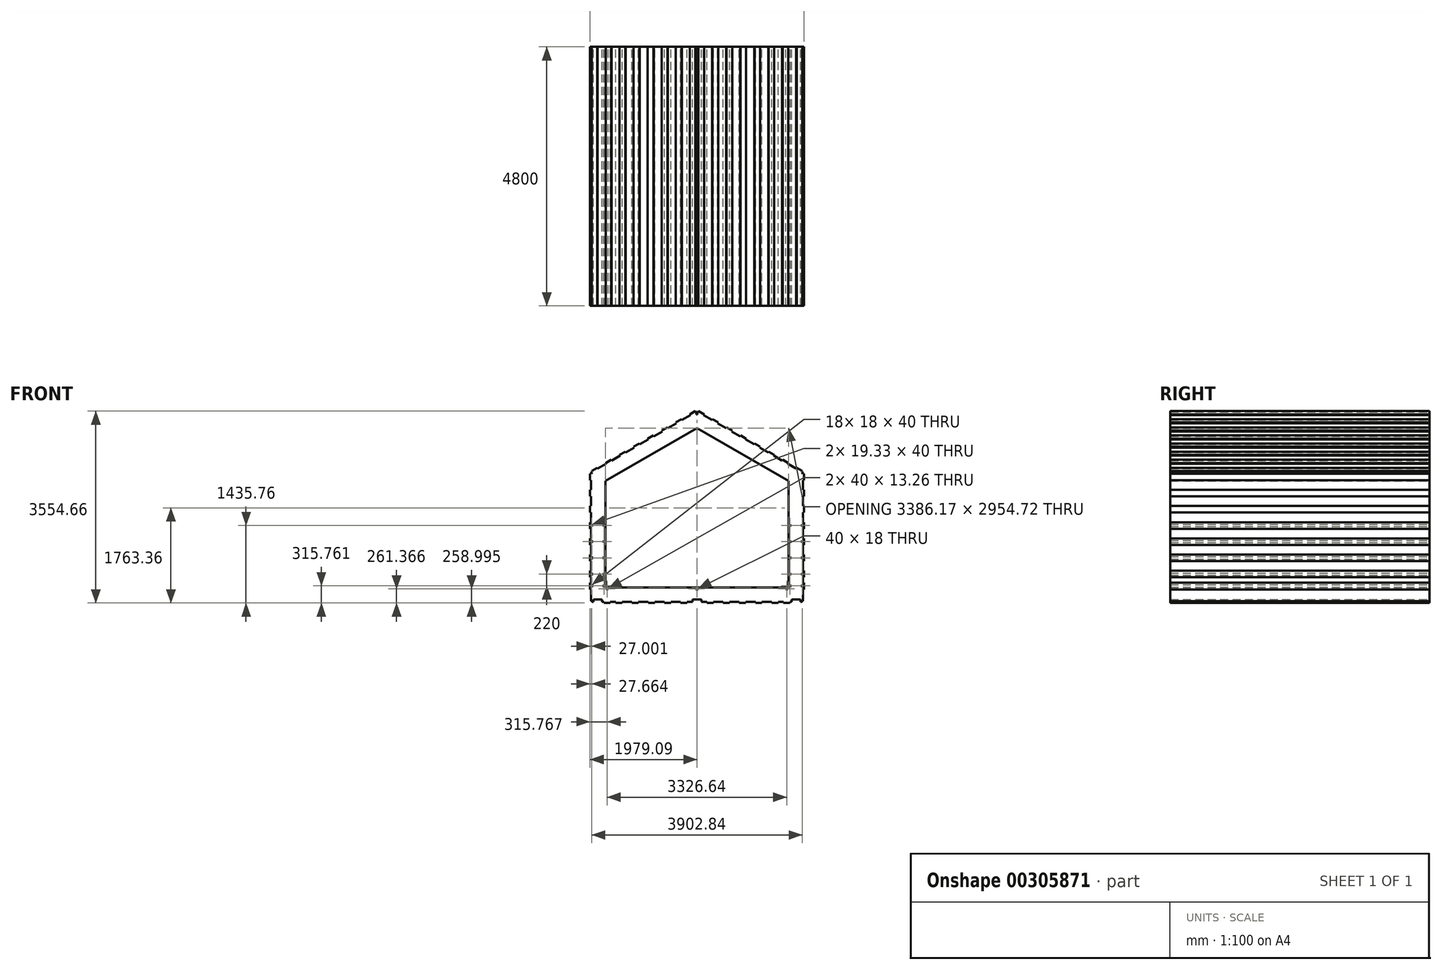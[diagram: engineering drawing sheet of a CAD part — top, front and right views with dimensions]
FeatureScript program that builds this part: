
annotation { "Feature Type Name" : "Feature", "Feature Type Description" : "" }
export const myFeature = defineFeature(function(context is Context, id is Id, definition is map)
    precondition{}
    {
        {
            var Q0;
            Q0=qCreatedBy(makeId("Front.planeOp"),FACE);
            var sketch = newSketch(context, id + "F0", { "sketchPlane" : qUnion([Q0])});
            skLineSegment(sketch, "E0", {"start": v(-1672.1, -978.06) * mm, "end": v(-1672.1, -1067.82) * mm});
            skLineSegment(sketch, "E1", {"start": v(-1672.1, -1067.82) * mm, "end": v(-1582.33, -1067.82) * mm});
            skLineSegment(sketch, "E2", {"start": v(-1582.33, -1067.82) * mm, "end": v(-1582.33, -1085.82) * mm});
            skLineSegment(sketch, "E3", {"start": v(-1582.33, -1085.82) * mm, "end": v(-1482.33, -1085.82) * mm});
            skLineSegment(sketch, "E4", {"start": v(-1482.33, -1085.82) * mm, "end": v(-1482.33, -1067.82) * mm});
            skLineSegment(sketch, "E5", {"start": v(-1482.33, -1067.82) * mm, "end": v(-1362.33, -1067.82) * mm});
            skLineSegment(sketch, "E6", {"start": v(-1362.33, -1067.82) * mm, "end": v(-1362.33, -1085.82) * mm});
            skLineSegment(sketch, "E7", {"start": v(-1362.33, -1085.82) * mm, "end": v(-1182.33, -1085.82) * mm});
            skLineSegment(sketch, "E8", {"start": v(-1182.33, -1085.82) * mm, "end": v(-1182.33, -1067.82) * mm});
            skLineSegment(sketch, "E9", {"start": v(-1182.33, -1067.82) * mm, "end": v(-1062.33, -1067.82) * mm});
            skLineSegment(sketch, "E10", {"start": v(-1062.33, -1067.82) * mm, "end": v(-1062.33, -1085.82) * mm});
            skLineSegment(sketch, "E11", {"start": v(-1062.33, -1085.82) * mm, "end": v(-882.33, -1085.82) * mm});
            skLineSegment(sketch, "E12", {"start": v(-882.33, -1085.82) * mm, "end": v(-882.33, -1067.82) * mm});
            skLineSegment(sketch, "E13", {"start": v(-882.33, -1067.82) * mm, "end": v(-762.33, -1067.82) * mm});
            skLineSegment(sketch, "E14", {"start": v(-762.33, -1067.82) * mm, "end": v(-762.33, -1085.82) * mm});
            skLineSegment(sketch, "E15", {"start": v(-762.33, -1085.82) * mm, "end": v(-582.33, -1085.82) * mm});
            skLineSegment(sketch, "E16", {"start": v(-582.33, -1085.82) * mm, "end": v(-582.33, -1067.82) * mm});
            skLineSegment(sketch, "E17", {"start": v(-582.33, -1067.82) * mm, "end": v(-462.33, -1067.82) * mm});
            skLineSegment(sketch, "E18", {"start": v(-462.33, -1067.82) * mm, "end": v(-462.33, -1085.82) * mm});
            skLineSegment(sketch, "E19", {"start": v(-462.33, -1085.82) * mm, "end": v(-282.33, -1085.82) * mm});
            skLineSegment(sketch, "E20", {"start": v(-282.33, -1085.82) * mm, "end": v(-282.33, -1067.82) * mm});
            skLineSegment(sketch, "E21", {"start": v(-282.33, -1067.82) * mm, "end": v(-162.33, -1067.82) * mm});
            skLineSegment(sketch, "E22", {"start": v(-162.33, -1067.82) * mm, "end": v(-162.33, -1085.82) * mm});
            skLineSegment(sketch, "E23", {"start": v(-162.33, -1085.82) * mm, "end": v(-39.02, -1085.82) * mm});
            skLineSegment(sketch, "E24", {"start": v(-39.02, -1085.82) * mm, "end": v(-39.02, -1067.82) * mm});
            skLineSegment(sketch, "E25", {"start": v(-39.02, -1067.82) * mm, "end": v(20.98, -1067.82) * mm});
            skLineSegment(sketch, "E26.bottom", {"start": v(0.98, -1085.82) * mm, "end": v(20.98, -1085.82) * mm});
            skLineSegment(sketch, "E26.top", {"start": v(0.98, -1103.82) * mm, "end": v(20.98, -1103.82) * mm});
            skLineSegment(sketch, "E26.left", {"start": v(0.98, -1085.82) * mm, "end": v(0.98, -1103.82) * mm});
            skLineSegment(sketch, "E26.right", {"start": v(20.98, -1085.82) * mm, "end": v(20.98, -1103.82) * mm});
            skLineSegment(sketch, "E27", {"start": v(-1672.1, -978.06) * mm, "end": v(-1690.1, -978.06) * mm});
            skLineSegment(sketch, "E28", {"start": v(-1690.1, -978.06) * mm, "end": v(-1690.1, -878.06) * mm});
            skLineSegment(sketch, "E29", {"start": v(-1690.1, -878.06) * mm, "end": v(-1672.1, -878.06) * mm});
            skLineSegment(sketch, "E30", {"start": v(-1672.1, -878.06) * mm, "end": v(-1672.1, -758.06) * mm});
            skLineSegment(sketch, "E31", {"start": v(-1672.1, -758.06) * mm, "end": v(-1690.1, -758.06) * mm});
            skLineSegment(sketch, "E32", {"start": v(-1690.1, -758.06) * mm, "end": v(-1690.1, -578.06) * mm});
            skLineSegment(sketch, "E33", {"start": v(-1690.1, -578.06) * mm, "end": v(-1672.1, -578.06) * mm});
            skLineSegment(sketch, "E34", {"start": v(-1672.1, -578.06) * mm, "end": v(-1672.1, -458.06) * mm});
            skLineSegment(sketch, "E35", {"start": v(-1672.1, -458.06) * mm, "end": v(-1690.1, -458.06) * mm});
            skLineSegment(sketch, "E36", {"start": v(-1690.1, -458.06) * mm, "end": v(-1690.1, -278.06) * mm});
            skLineSegment(sketch, "E37.bottom", {"start": v(-1690.1, -1018.06) * mm, "end": v(-1708.1, -1018.06) * mm});
            skLineSegment(sketch, "E37.top", {"start": v(-1690.1, -1058.06) * mm, "end": v(-1708.1, -1058.06) * mm});
            skLineSegment(sketch, "E37.left", {"start": v(-1690.1, -1018.06) * mm, "end": v(-1690.1, -1058.06) * mm});
            skLineSegment(sketch, "E37.right", {"start": v(-1708.1, -1018.06) * mm, "end": v(-1708.1, -1058.06) * mm});
            skLineSegment(sketch, "E38.bottom", {"start": v(-1622.33, -1085.82) * mm, "end": v(-1662.33, -1085.82) * mm});
            skLineSegment(sketch, "E38.top", {"start": v(-1622.33, -1099.08) * mm, "end": v(-1662.33, -1099.08) * mm});
            skLineSegment(sketch, "E38.left", {"start": v(-1622.33, -1085.82) * mm, "end": v(-1622.33, -1099.08) * mm});
            skLineSegment(sketch, "E38.right", {"start": v(-1662.33, -1085.82) * mm, "end": v(-1662.33, -1099.08) * mm});
            skLineSegment(sketch, "E39", {"start": v(-1690.1, -978.06) * mm, "end": v(-1940.1, -978.06) * mm, "construction": true});
            skLineSegment(sketch, "E40", {"start": v(-1940.1, -978.06) * mm, "end": v(-1958.1, -978.06) * mm});
            skLineSegment(sketch, "E41", {"start": v(-1958.1, -978.06) * mm, "end": v(-1958.1, -1103.83) * mm});
            skLineSegment(sketch, "E42", {"start": v(-1940.1, -978.06) * mm, "end": v(-1940.1, -878.06) * mm});
            skLineSegment(sketch, "E43", {"start": v(-1940.1, -878.06) * mm, "end": v(-1958.1, -878.06) * mm});
            skLineSegment(sketch, "E44.bottom", {"start": v(-1940.1, -1018.06) * mm, "end": v(-1922.1, -1018.06) * mm});
            skLineSegment(sketch, "E44.top", {"start": v(-1940.1, -1058.06) * mm, "end": v(-1922.1, -1058.06) * mm});
            skLineSegment(sketch, "E44.left", {"start": v(-1940.1, -1018.06) * mm, "end": v(-1940.1, -1058.06) * mm});
            skLineSegment(sketch, "E44.right", {"start": v(-1922.1, -1018.06) * mm, "end": v(-1922.1, -1058.06) * mm});
            skLineSegment(sketch, "E45", {"start": v(-1958.1, -878.06) * mm, "end": v(-1958.1, -758.06) * mm});
            skLineSegment(sketch, "E46", {"start": v(-1958.1, -758.06) * mm, "end": v(-1940.1, -758.06) * mm});
            skLineSegment(sketch, "E47.bottom", {"start": v(-1940.1, -838.06) * mm, "end": v(-1922.1, -838.06) * mm});
            skLineSegment(sketch, "E47.top", {"start": v(-1940.1, -798.06) * mm, "end": v(-1922.1, -798.06) * mm});
            skLineSegment(sketch, "E47.left", {"start": v(-1940.1, -838.06) * mm, "end": v(-1940.1, -798.06) * mm});
            skLineSegment(sketch, "E47.right", {"start": v(-1922.1, -838.06) * mm, "end": v(-1922.1, -798.06) * mm});
            skLineSegment(sketch, "E48", {"start": v(-1940.1, -758.06) * mm, "end": v(-1940.1, -578.06) * mm});
            skLineSegment(sketch, "E49", {"start": v(-1940.1, -578.06) * mm, "end": v(-1958.1, -578.06) * mm});
            skLineSegment(sketch, "E50.bottom", {"start": v(-1690.1, -798.06) * mm, "end": v(-1708.1, -798.06) * mm});
            skLineSegment(sketch, "E50.top", {"start": v(-1690.1, -838.06) * mm, "end": v(-1708.1, -838.06) * mm});
            skLineSegment(sketch, "E50.left", {"start": v(-1690.1, -798.06) * mm, "end": v(-1690.1, -838.06) * mm});
            skLineSegment(sketch, "E50.right", {"start": v(-1708.1, -798.06) * mm, "end": v(-1708.1, -838.06) * mm});
            skLineSegment(sketch, "E51", {"start": v(-1958.1, -578.06) * mm, "end": v(-1958.1, -458.06) * mm});
            skLineSegment(sketch, "E52", {"start": v(-1958.1, -458.06) * mm, "end": v(-1940.1, -458.06) * mm});
            skLineSegment(sketch, "E53", {"start": v(-1940.1, -458.06) * mm, "end": v(-1940.1, -278.06) * mm});
            skLineSegment(sketch, "E54.bottom", {"start": v(-1940.1, -538.06) * mm, "end": v(-1922.1, -538.06) * mm});
            skLineSegment(sketch, "E54.top", {"start": v(-1940.1, -498.06) * mm, "end": v(-1922.1, -498.06) * mm});
            skLineSegment(sketch, "E54.left", {"start": v(-1940.1, -538.06) * mm, "end": v(-1940.1, -498.06) * mm});
            skLineSegment(sketch, "E54.right", {"start": v(-1922.1, -538.06) * mm, "end": v(-1922.1, -498.06) * mm});
            skLineSegment(sketch, "E55.bottom", {"start": v(-1690.1, -538.06) * mm, "end": v(-1708.1, -538.06) * mm});
            skLineSegment(sketch, "E55.top", {"start": v(-1690.1, -498.06) * mm, "end": v(-1708.1, -498.06) * mm});
            skLineSegment(sketch, "E55.left", {"start": v(-1690.1, -538.06) * mm, "end": v(-1690.1, -498.06) * mm});
            skLineSegment(sketch, "E55.right", {"start": v(-1708.1, -538.06) * mm, "end": v(-1708.1, -498.06) * mm});
            skLineSegment(sketch, "E56", {"start": v(-1940.1, -278.06) * mm, "end": v(-1958.1, -278.06) * mm});
            skLineSegment(sketch, "E57", {"start": v(-1958.1, -278.06) * mm, "end": v(-1958.1, -158.06) * mm});
            skLineSegment(sketch, "E58", {"start": v(-1690.1, -278.06) * mm, "end": v(-1672.1, -278.06) * mm});
            skLineSegment(sketch, "E59", {"start": v(-1672.1, -278.06) * mm, "end": v(-1672.1, -158.06) * mm});
            skLineSegment(sketch, "E60.bottom", {"start": v(-1940.1, -238.06) * mm, "end": v(-1922.1, -238.06) * mm});
            skLineSegment(sketch, "E60.top", {"start": v(-1940.1, -198.06) * mm, "end": v(-1922.1, -198.06) * mm});
            skLineSegment(sketch, "E60.left", {"start": v(-1940.1, -238.06) * mm, "end": v(-1940.1, -198.06) * mm});
            skLineSegment(sketch, "E60.right", {"start": v(-1922.1, -238.06) * mm, "end": v(-1922.1, -198.06) * mm});
            skLineSegment(sketch, "E61.bottom", {"start": v(-1690.1, -238.06) * mm, "end": v(-1708.1, -238.06) * mm});
            skLineSegment(sketch, "E61.top", {"start": v(-1690.1, -198.06) * mm, "end": v(-1708.1, -198.06) * mm});
            skLineSegment(sketch, "E61.left", {"start": v(-1690.1, -238.06) * mm, "end": v(-1690.1, -198.06) * mm});
            skLineSegment(sketch, "E61.right", {"start": v(-1708.1, -238.06) * mm, "end": v(-1708.1, -198.06) * mm});
            skLineSegment(sketch, "E62", {"start": v(-1958.1, -158.06) * mm, "end": v(-1940.1, -158.06) * mm});
            skPoint(sketch, "E62.endSnap0", {"position": v(-1940.1, -218.06) * mm});
            skLineSegment(sketch, "E63", {"start": v(-1672.1, -158.06) * mm, "end": v(-1690.1, -158.06) * mm});
            skPoint(sketch, "E63.endSnap0", {"position": v(-1690.1, -218.06) * mm});
            skLineSegment(sketch, "E64", {"start": v(-1940.1, -158.06) * mm, "end": v(-1940.1, 21.94) * mm});
            skLineSegment(sketch, "E65", {"start": v(-1690.1, -158.06) * mm, "end": v(-1690.1, 21.94) * mm});
            skLineSegment(sketch, "E66", {"start": v(-1690.1, 21.94) * mm, "end": v(-1672.1, 21.94) * mm});
            skLineSegment(sketch, "E67", {"start": v(-1672.1, 21.94) * mm, "end": v(-1672.1, 141.94) * mm});
            skLineSegment(sketch, "E68", {"start": v(-1672.1, 141.94) * mm, "end": v(-1690.1, 141.94) * mm});
            skLineSegment(sketch, "E69", {"start": v(-1690.1, 141.94) * mm, "end": v(-1690.1, 321.94) * mm});
            skLineSegment(sketch, "E70", {"start": v(-1940.1, 21.94) * mm, "end": v(-1958.1, 21.94) * mm});
            skLineSegment(sketch, "E71", {"start": v(-1958.1, 21.94) * mm, "end": v(-1958.1, 141.94) * mm});
            skLineSegment(sketch, "E72", {"start": v(-1958.1, 141.94) * mm, "end": v(-1940.1, 141.94) * mm});
            skLineSegment(sketch, "E73", {"start": v(-1940.1, 141.94) * mm, "end": v(-1940.1, 321.94) * mm});
            skLineSegment(sketch, "E74.bottom", {"start": v(-1940.1, 61.94) * mm, "end": v(-1920.77, 61.94) * mm});
            skLineSegment(sketch, "E74.top", {"start": v(-1940.1, 101.94) * mm, "end": v(-1920.77, 101.94) * mm});
            skLineSegment(sketch, "E74.left", {"start": v(-1940.1, 61.94) * mm, "end": v(-1940.1, 101.94) * mm});
            skLineSegment(sketch, "E74.right", {"start": v(-1920.77, 61.94) * mm, "end": v(-1920.77, 101.94) * mm});
            skLineSegment(sketch, "E75.bottom", {"start": v(-1690.1, 61.94) * mm, "end": v(-1708.1, 61.94) * mm});
            skLineSegment(sketch, "E75.top", {"start": v(-1690.1, 101.94) * mm, "end": v(-1708.1, 101.94) * mm});
            skLineSegment(sketch, "E75.left", {"start": v(-1690.1, 61.94) * mm, "end": v(-1690.1, 101.94) * mm});
            skLineSegment(sketch, "E75.right", {"start": v(-1708.1, 61.94) * mm, "end": v(-1708.1, 101.94) * mm});
            skLineSegment(sketch, "E76", {"start": v(-1940.1, 321.94) * mm, "end": v(-1958.1, 321.94) * mm});
            skLineSegment(sketch, "E77", {"start": v(-1958.1, 321.94) * mm, "end": v(-1958.1, 441.94) * mm});
            skLineSegment(sketch, "E78", {"start": v(-1690.1, 321.94) * mm, "end": v(-1672.1, 321.94) * mm});
            skLineSegment(sketch, "E79", {"start": v(-1672.1, 321.94) * mm, "end": v(-1672.1, 441.94) * mm});
            skLineSegment(sketch, "E80", {"start": v(-1958.1, 441.94) * mm, "end": v(-1940.1, 441.94) * mm});
            skLineSegment(sketch, "E81", {"start": v(-1940.1, 441.94) * mm, "end": v(-1940.1, 621.94) * mm});
            skLineSegment(sketch, "E82", {"start": v(-1672.1, 441.94) * mm, "end": v(-1690.1, 441.94) * mm});
            skLineSegment(sketch, "E83", {"start": v(-1690.1, 441.94) * mm, "end": v(-1690.1, 621.94) * mm});
            skLineSegment(sketch, "E84", {"start": v(-1940.1, 621.94) * mm, "end": v(-1958.1, 621.94) * mm});
            skLineSegment(sketch, "E85", {"start": v(-1958.1, 621.94) * mm, "end": v(-1958.1, 741.94) * mm});
            skLineSegment(sketch, "E86", {"start": v(-1958.1, 741.94) * mm, "end": v(-1940.1, 741.94) * mm});
            skLineSegment(sketch, "E87", {"start": v(-1690.1, 621.94) * mm, "end": v(-1672.1, 621.94) * mm});
            skLineSegment(sketch, "E88", {"start": v(-1672.1, 621.94) * mm, "end": v(-1672.1, 741.94) * mm});
            skLineSegment(sketch, "E89", {"start": v(-1672.1, 741.94) * mm, "end": v(-1690.1, 741.94) * mm});
            skLineSegment(sketch, "E90", {"start": v(-1940.1, 741.94) * mm, "end": v(-1940.1, 921.94) * mm});
            skLineSegment(sketch, "E91", {"start": v(-1940.1, 921.94) * mm, "end": v(-1958.1, 921.94) * mm});
            skLineSegment(sketch, "E92", {"start": v(-1958.1, 921.94) * mm, "end": v(-1958.1, 1041.94) * mm});
            skLineSegment(sketch, "E93", {"start": v(-1958.1, 1041.94) * mm, "end": v(-1940.1, 1041.94) * mm});
            skLineSegment(sketch, "E94", {"start": v(-1940.1, 1041.94) * mm, "end": v(-1940.1, 1064.17) * mm});
            skLineSegment(sketch, "E95", {"start": v(-1940.1, 1041.94) * mm, "end": v(-1920.84, 1075.29) * mm});
            skLineSegment(sketch, "E96", {"start": v(-1940.1, 1064.17) * mm, "end": v(-1920.84, 1075.29) * mm});
            skLineSegment(sketch, "E97", {"start": v(-1920.84, 1075.29) * mm, "end": v(-1929.84, 1090.88) * mm});
            skLineSegment(sketch, "E98", {"start": v(-1929.84, 1090.88) * mm, "end": v(-1825.92, 1150.87) * mm});
            skLineSegment(sketch, "E99", {"start": v(-1825.92, 1150.87) * mm, "end": v(-1816.92, 1135.28) * mm});
            skLineSegment(sketch, "E100", {"start": v(-1816.92, 1135.28) * mm, "end": v(-1661.03, 1225.28) * mm});
            skLineSegment(sketch, "E101", {"start": v(-1661.03, 1225.28) * mm, "end": v(-1670.03, 1240.87) * mm});
            skLineSegment(sketch, "E102", {"start": v(-1670.03, 1240.87) * mm, "end": v(-1566.1, 1300.87) * mm});
            skLineSegment(sketch, "E103", {"start": v(-1566.1, 1300.87) * mm, "end": v(-1557.1, 1285.28) * mm});
            skLineSegment(sketch, "E104", {"start": v(-1661.03, 1225.28) * mm, "end": v(-1536.04, 1008.77) * mm, "construction": true});
            skLineSegment(sketch, "E105", {"start": v(-1536.04, 1008.77) * mm, "end": v(-1527.04, 993.18) * mm});
            skLineSegment(sketch, "E106", {"start": v(-1527.04, 993.18) * mm, "end": v(-1423.11, 1053.18) * mm});
            skLineSegment(sketch, "E107", {"start": v(-1423.11, 1053.18) * mm, "end": v(-1432.11, 1068.77) * mm});
            skLineSegment(sketch, "E108", {"start": v(-1690.1, 741.94) * mm, "end": v(-1690.1, 919.83) * mm});
            skLineSegment(sketch, "E109", {"start": v(-1536.04, 1008.77) * mm, "end": v(-1690.1, 919.83) * mm});
            skLineSegment(sketch, "E110", {"start": v(-1557.1, 1285.28) * mm, "end": v(-1401.22, 1375.28) * mm});
            skLineSegment(sketch, "E111", {"start": v(-1432.11, 1068.77) * mm, "end": v(-1276.23, 1158.77) * mm});
            skLineSegment(sketch, "E112", {"start": v(-1401.22, 1375.28) * mm, "end": v(-1410.22, 1390.86) * mm});
            skLineSegment(sketch, "E113", {"start": v(-1410.22, 1390.86) * mm, "end": v(-1306.3, 1450.86) * mm});
            skLineSegment(sketch, "E114", {"start": v(-1276.23, 1158.77) * mm, "end": v(-1267.23, 1143.18) * mm});
            skLineSegment(sketch, "E115", {"start": v(-1267.23, 1143.18) * mm, "end": v(-1163.3, 1203.18) * mm});
            skLineSegment(sketch, "E116", {"start": v(-1163.3, 1203.18) * mm, "end": v(-1172.3, 1218.77) * mm});
            skLineSegment(sketch, "E117", {"start": v(-1172.3, 1218.77) * mm, "end": v(-1016.42, 1308.76) * mm});
            skLineSegment(sketch, "E118", {"start": v(-1306.3, 1450.86) * mm, "end": v(-1297.3, 1435.27) * mm});
            skLineSegment(sketch, "E119", {"start": v(-1297.3, 1435.27) * mm, "end": v(-1141.41, 1525.27) * mm});
            skLineSegment(sketch, "E120", {"start": v(-1141.41, 1525.27) * mm, "end": v(-1150.41, 1540.86) * mm});
            skLineSegment(sketch, "E121", {"start": v(-1150.41, 1540.86) * mm, "end": v(-1046.49, 1600.86) * mm});
            skLineSegment(sketch, "E122", {"start": v(-1016.42, 1308.76) * mm, "end": v(-1007.42, 1293.17) * mm});
            skLineSegment(sketch, "E123", {"start": v(-1007.42, 1293.17) * mm, "end": v(-903.5, 1353.17) * mm});
            skLineSegment(sketch, "E124", {"start": v(-1046.49, 1600.86) * mm, "end": v(-1037.49, 1585.27) * mm});
            skLineSegment(sketch, "E125", {"start": v(-1037.49, 1585.27) * mm, "end": v(-881.6, 1675.27) * mm});
            skLineSegment(sketch, "E126", {"start": v(-903.5, 1353.17) * mm, "end": v(-912.5, 1368.76) * mm});
            skLineSegment(sketch, "E127", {"start": v(-912.5, 1368.76) * mm, "end": v(-756.6, 1458.76) * mm});
            skLineSegment(sketch, "E128", {"start": v(-881.6, 1675.27) * mm, "end": v(-890.6, 1690.85) * mm});
            skLineSegment(sketch, "E129", {"start": v(-890.6, 1690.85) * mm, "end": v(-786.68, 1750.85) * mm});
            skLineSegment(sketch, "E130", {"start": v(-756.6, 1458.76) * mm, "end": v(-747.6, 1443.17) * mm});
            skLineSegment(sketch, "E131", {"start": v(-747.6, 1443.17) * mm, "end": v(-643.68, 1503.17) * mm});
            skLineSegment(sketch, "E132", {"start": v(-786.68, 1750.85) * mm, "end": v(-777.68, 1735.26) * mm});
            skLineSegment(sketch, "E133", {"start": v(-777.68, 1735.26) * mm, "end": v(-621.8, 1825.26) * mm});
            skLineSegment(sketch, "E134", {"start": v(-621.8, 1825.26) * mm, "end": v(-630.8, 1840.85) * mm});
            skLineSegment(sketch, "E135", {"start": v(-630.8, 1840.85) * mm, "end": v(-526.87, 1900.85) * mm});
            skLineSegment(sketch, "E136", {"start": v(-526.87, 1900.85) * mm, "end": v(-517.87, 1885.26) * mm});
            skLineSegment(sketch, "E137", {"start": v(-517.87, 1885.26) * mm, "end": v(-361.98, 1975.26) * mm});
            skLineSegment(sketch, "E138", {"start": v(-361.98, 1975.26) * mm, "end": v(-370.98, 1990.84) * mm});
            skLineSegment(sketch, "E139", {"start": v(-370.98, 1990.84) * mm, "end": v(-267.06, 2050.84) * mm});
            skLineSegment(sketch, "E140", {"start": v(-267.06, 2050.84) * mm, "end": v(-258.06, 2035.25) * mm});
            skLineSegment(sketch, "E141", {"start": v(-258.06, 2035.25) * mm, "end": v(-102.17, 2125.25) * mm});
            skLineSegment(sketch, "E142", {"start": v(-102.17, 2125.25) * mm, "end": v(-111.17, 2140.84) * mm});
            skLineSegment(sketch, "E143", {"start": v(-111.17, 2140.84) * mm, "end": v(-7.25, 2200.84) * mm});
            skLineSegment(sketch, "E144", {"start": v(-643.68, 1503.17) * mm, "end": v(-652.68, 1518.75) * mm});
            skLineSegment(sketch, "E145", {"start": v(-652.68, 1518.75) * mm, "end": v(-496.8, 1608.75) * mm});
            skLineSegment(sketch, "E146", {"start": v(-496.8, 1608.75) * mm, "end": v(-487.8, 1593.16) * mm});
            skLineSegment(sketch, "E147", {"start": v(-487.8, 1593.16) * mm, "end": v(-383.87, 1653.16) * mm});
            skLineSegment(sketch, "E148", {"start": v(-383.87, 1653.16) * mm, "end": v(-392.87, 1668.75) * mm});
            skLineSegment(sketch, "E149", {"start": v(-392.87, 1668.75) * mm, "end": v(-236.99, 1758.75) * mm});
            skLineSegment(sketch, "E150", {"start": v(-236.99, 1758.75) * mm, "end": v(-227.99, 1743.16) * mm});
            skLineSegment(sketch, "E151", {"start": v(-227.99, 1743.16) * mm, "end": v(-124.06, 1803.16) * mm});
            skLineSegment(sketch, "E152", {"start": v(-124.06, 1803.16) * mm, "end": v(-133.06, 1818.74) * mm});
            skLineSegment(sketch, "E153", {"start": v(-133.06, 1818.74) * mm, "end": v(21, 1907.69) * mm});
            skLineSegment(sketch, "E154", {"start": v(-7.25, 2200.84) * mm, "end": v(1.75, 2185.25) * mm});
            skLineSegment(sketch, "E155", {"start": v(1.75, 2185.25) * mm, "end": v(12, 2191.16) * mm});
            skLineSegment(sketch, "E156", {"start": v(12, 2191.16) * mm, "end": v(12, 2141.17) * mm});
            skLineSegment(sketch, "E157", {"start": v(12, 2141.17) * mm, "end": v(21, 2141.17) * mm});
            skLineSegment(sketch, "E158", {"start": v(-621.8, 1825.26) * mm, "end": v(-496.8, 1608.75) * mm, "construction": true});
            skLineSegment(sketch, "E159", {"start": v(-162.33, -1335.82) * mm, "end": v(-162.33, -1353.82) * mm});
            skLineSegment(sketch, "E160", {"start": v(-162.33, -1353.82) * mm, "end": v(-282.33, -1353.82) * mm});
            skLineSegment(sketch, "E161", {"start": v(-282.33, -1353.82) * mm, "end": v(-282.33, -1335.82) * mm});
            skLineSegment(sketch, "E162", {"start": v(-282.33, -1335.82) * mm, "end": v(-462.33, -1335.82) * mm});
            skLineSegment(sketch, "E163", {"start": v(-462.33, -1335.82) * mm, "end": v(-462.33, -1353.82) * mm});
            skLineSegment(sketch, "E164", {"start": v(-462.33, -1353.82) * mm, "end": v(-582.33, -1353.82) * mm});
            skLineSegment(sketch, "E165", {"start": v(-582.33, -1353.82) * mm, "end": v(-582.33, -1335.82) * mm});
            skLineSegment(sketch, "E166", {"start": v(-582.33, -1335.82) * mm, "end": v(-762.33, -1335.82) * mm});
            skLineSegment(sketch, "E167", {"start": v(-762.33, -1335.82) * mm, "end": v(-762.33, -1353.82) * mm});
            skLineSegment(sketch, "E168", {"start": v(-762.33, -1353.82) * mm, "end": v(-882.33, -1353.82) * mm});
            skLineSegment(sketch, "E169", {"start": v(-882.33, -1353.82) * mm, "end": v(-882.33, -1335.82) * mm});
            skLineSegment(sketch, "E170", {"start": v(-882.33, -1335.82) * mm, "end": v(-1062.33, -1335.82) * mm});
            skLineSegment(sketch, "E171", {"start": v(-1062.33, -1335.82) * mm, "end": v(-1062.33, -1353.82) * mm});
            skLineSegment(sketch, "E172", {"start": v(-1062.33, -1353.82) * mm, "end": v(-1182.33, -1353.82) * mm});
            skLineSegment(sketch, "E173", {"start": v(-1182.33, -1353.82) * mm, "end": v(-1182.33, -1335.82) * mm});
            skLineSegment(sketch, "E174", {"start": v(-1182.33, -1335.82) * mm, "end": v(-1362.33, -1335.82) * mm});
            skLineSegment(sketch, "E175", {"start": v(-1362.33, -1335.82) * mm, "end": v(-1362.33, -1353.82) * mm});
            skLineSegment(sketch, "E176", {"start": v(-1362.33, -1353.82) * mm, "end": v(-1482.33, -1353.82) * mm});
            skLineSegment(sketch, "E177", {"start": v(-1482.33, -1353.82) * mm, "end": v(-1482.33, -1335.82) * mm});
            skLineSegment(sketch, "E178", {"start": v(-1482.33, -1335.82) * mm, "end": v(-1582.33, -1335.82) * mm});
            skLineSegment(sketch, "E179", {"start": v(-1582.33, -1335.82) * mm, "end": v(-1582.33, -1353.82) * mm});
            skLineSegment(sketch, "E180", {"start": v(-1582.33, -1353.82) * mm, "end": v(-1702.33, -1353.82) * mm});
            skLineSegment(sketch, "E181", {"start": v(-1702.33, -1353.82) * mm, "end": v(-1702.33, -1335.82) * mm});
            skLineSegment(sketch, "E182", {"start": v(-1702.33, -1335.82) * mm, "end": v(-1735.1, -1335.82) * mm});
            skLineSegment(sketch, "E183", {"start": v(-1735.1, -1335.82) * mm, "end": v(-1735.1, -1285.82) * mm});
            skLineSegment(sketch, "E184", {"start": v(-1735.1, -1285.82) * mm, "end": v(-1895.1, -1285.82) * mm});
            skLineSegment(sketch, "E185", {"start": v(-1895.1, -1285.82) * mm, "end": v(-1895.1, -1335.82) * mm});
            skLineSegment(sketch, "E186", {"start": v(-1895.1, -1335.82) * mm, "end": v(-1920.1, -1335.82) * mm});
            skLineSegment(sketch, "E187", {"start": v(-1920.1, -1335.82) * mm, "end": v(-1920.1, -1317.82) * mm});
            skLineSegment(sketch, "E188", {"start": v(-1920.1, -1317.82) * mm, "end": v(-1940.1, -1317.82) * mm});
            skLineSegment(sketch, "E189", {"start": v(-1940.1, -1317.82) * mm, "end": v(-1940.1, -1103.83) * mm});
            skLineSegment(sketch, "E190", {"start": v(-1940.1, -1103.83) * mm, "end": v(-1958.1, -1103.83) * mm});
            skLineSegment(sketch, "E191", {"start": v(20.98, -1593.05) * mm, "end": v(20.98, 2406.95) * mm, "construction": true});
            skLineSegment(sketch, "E192", {"start": v(-162.33, -1335.82) * mm, "end": v(-59.01, -1335.82) * mm});
            skLineSegment(sketch, "E193", {"start": v(-59.01, -1335.82) * mm, "end": v(-59.01, -1285.82) * mm});
            skLineSegment(sketch, "E194", {"start": v(-59.01, -1285.82) * mm, "end": v(20.98, -1285.82) * mm});
            skLineSegment(sketch, "E195.MirrorCS", {"start": v(1982.07, -198.06) * mm, "end": v(1964.07, -198.06) * mm});
            skLineSegment(sketch, "E196.MirrorCS", {"start": v(1982.07, 1064.17) * mm, "end": v(1962.81, 1075.29) * mm});
            skLineSegment(sketch, "E197.MirrorCS", {"start": v(1982.07, -238.06) * mm, "end": v(1964.07, -238.06) * mm});
            skLineSegment(sketch, "E198.MirrorCS", {"start": v(1732.07, -198.06) * mm, "end": v(1750.07, -198.06) * mm});
            skLineSegment(sketch, "E199.MirrorCS", {"start": v(2000.07, 1041.94) * mm, "end": v(1982.07, 1041.94) * mm});
            skLineSegment(sketch, "E200.MirrorCS", {"start": v(1732.07, -238.06) * mm, "end": v(1750.07, -238.06) * mm});
            skLineSegment(sketch, "E201.MirrorCS", {"start": v(1982.07, -278.06) * mm, "end": v(2000.07, -278.06) * mm});
            skLineSegment(sketch, "E202.MirrorCS", {"start": v(1982.07, -238.06) * mm, "end": v(1982.07, -198.06) * mm});
            skLineSegment(sketch, "E203.MirrorCS", {"start": v(1962.81, 1075.29) * mm, "end": v(1971.81, 1090.88) * mm});
            skLineSegment(sketch, "E204.MirrorCS", {"start": v(2000.07, -158.06) * mm, "end": v(1982.07, -158.06) * mm});
            skLineSegment(sketch, "E205.MirrorCS", {"start": v(1982.07, -838.06) * mm, "end": v(1964.07, -838.06) * mm});
            skLineSegment(sketch, "E206.MirrorCS", {"start": v(2000.07, -278.06) * mm, "end": v(2000.07, -158.06) * mm});
            skLineSegment(sketch, "E207.MirrorCS", {"start": v(80.98, -1085.82) * mm, "end": v(80.98, -1067.82) * mm});
            skLineSegment(sketch, "E208.MirrorCS", {"start": v(1867.89, 1150.87) * mm, "end": v(1858.89, 1135.28) * mm});
            skLineSegment(sketch, "E209.MirrorCS", {"start": v(1964.07, -238.06) * mm, "end": v(1964.07, -198.06) * mm});
            skLineSegment(sketch, "E210.MirrorCS", {"start": v(1732.07, -278.06) * mm, "end": v(1714.07, -278.06) * mm});
            skLineSegment(sketch, "E211.MirrorCS", {"start": v(1971.81, 1090.88) * mm, "end": v(1867.89, 1150.87) * mm});
            skLineSegment(sketch, "E212.MirrorCS", {"start": v(1982.07, -1058.06) * mm, "end": v(1964.07, -1058.06) * mm});
            skLineSegment(sketch, "E213.MirrorCS", {"start": v(1982.07, -1018.06) * mm, "end": v(1964.07, -1018.06) * mm});
            skLineSegment(sketch, "E214.MirrorCS", {"start": v(1982.07, -798.06) * mm, "end": v(1964.07, -798.06) * mm});
            skLineSegment(sketch, "E215.MirrorCS", {"start": v(1714.07, -158.06) * mm, "end": v(1732.07, -158.06) * mm});
            skLineSegment(sketch, "E216.MirrorCS", {"start": v(1982.07, -838.06) * mm, "end": v(1982.07, -798.06) * mm});
            skLineSegment(sketch, "E217.MirrorCS", {"start": v(1750.07, -238.06) * mm, "end": v(1750.07, -198.06) * mm});
            skLineSegment(sketch, "E218.MirrorCS", {"start": v(40.98, -1103.82) * mm, "end": v(20.98, -1103.82) * mm});
            skLineSegment(sketch, "E219.MirrorCS", {"start": v(1982.07, 1041.94) * mm, "end": v(1982.07, 1064.17) * mm});
            skLineSegment(sketch, "E220.MirrorCS", {"start": v(1982.07, 1041.94) * mm, "end": v(1962.81, 1075.29) * mm});
            skLineSegment(sketch, "E221.MirrorCS", {"start": v(1714.07, -278.06) * mm, "end": v(1714.07, -158.06) * mm});
            skLineSegment(sketch, "E222.MirrorCS", {"start": v(1732.07, -238.06) * mm, "end": v(1732.07, -198.06) * mm});
            skLineSegment(sketch, "E223.MirrorCS", {"start": v(40.98, -1085.82) * mm, "end": v(20.98, -1085.82) * mm});
            skLineSegment(sketch, "E224.MirrorCS", {"start": v(1982.07, -498.06) * mm, "end": v(1964.07, -498.06) * mm});
            skLineSegment(sketch, "E225.MirrorCS", {"start": v(1982.07, 101.94) * mm, "end": v(1962.74, 101.94) * mm});
            skLineSegment(sketch, "E226.MirrorCS", {"start": v(80.98, -1067.82) * mm, "end": v(20.98, -1067.82) * mm});
            skLineSegment(sketch, "E227.MirrorCS", {"start": v(1732.07, -1058.06) * mm, "end": v(1750.07, -1058.06) * mm});
            skLineSegment(sketch, "E228.MirrorCS", {"start": v(2000.07, -878.06) * mm, "end": v(2000.07, -758.06) * mm});
            skLineSegment(sketch, "E229.MirrorCS", {"start": v(1982.07, -978.06) * mm, "end": v(2000.07, -978.06) * mm});
            skLineSegment(sketch, "E230.MirrorCS", {"start": v(1982.07, -538.06) * mm, "end": v(1964.07, -538.06) * mm});
            skLineSegment(sketch, "E231.MirrorCS", {"start": v(1982.07, 61.94) * mm, "end": v(1962.74, 61.94) * mm});
            skLineSegment(sketch, "E232.MirrorCS", {"start": v(1732.07, -1018.06) * mm, "end": v(1750.07, -1018.06) * mm});
            skLineSegment(sketch, "E233.MirrorCS", {"start": v(1982.07, -1018.06) * mm, "end": v(1982.07, -1058.06) * mm});
            skLineSegment(sketch, "E234.MirrorCS", {"start": v(1704.3, -1085.82) * mm, "end": v(1704.3, -1099.08) * mm});
            skLineSegment(sketch, "E235.MirrorCS", {"start": v(1714.07, -978.06) * mm, "end": v(1732.07, -978.06) * mm});
            skLineSegment(sketch, "E236.MirrorCS", {"start": v(1964.07, -838.06) * mm, "end": v(1964.07, -798.06) * mm});
            skLineSegment(sketch, "E237.MirrorCS", {"start": v(40.98, -1085.82) * mm, "end": v(40.98, -1103.82) * mm});
            skLineSegment(sketch, "E238.MirrorCS", {"start": v(1664.3, -1099.08) * mm, "end": v(1704.3, -1099.08) * mm});
            skLineSegment(sketch, "E239.MirrorCS", {"start": v(1750.07, -798.06) * mm, "end": v(1750.07, -838.06) * mm});
            skLineSegment(sketch, "E240.MirrorCS", {"start": v(1982.07, -878.06) * mm, "end": v(2000.07, -878.06) * mm});
            skLineSegment(sketch, "E241.MirrorCS", {"start": v(1982.07, -978.06) * mm, "end": v(1982.07, -878.06) * mm});
            skLineSegment(sketch, "E242.MirrorCS", {"start": v(1732.07, -798.06) * mm, "end": v(1732.07, -838.06) * mm});
            skLineSegment(sketch, "E243.MirrorCS", {"start": v(2000.07, -758.06) * mm, "end": v(1982.07, -758.06) * mm});
            skLineSegment(sketch, "E244.MirrorCS", {"start": v(1714.07, -758.06) * mm, "end": v(1732.07, -758.06) * mm});
            skLineSegment(sketch, "E245.MirrorCS", {"start": v(1982.07, -1103.83) * mm, "end": v(2000.07, -1103.83) * mm});
            skLineSegment(sketch, "E246.MirrorCS", {"start": v(1714.07, -878.06) * mm, "end": v(1714.07, -758.06) * mm});
            skLineSegment(sketch, "E247.MirrorCS", {"start": v(1732.07, -798.06) * mm, "end": v(1750.07, -798.06) * mm});
            skLineSegment(sketch, "E248.MirrorCS", {"start": v(1732.07, -878.06) * mm, "end": v(1714.07, -878.06) * mm});
            skLineSegment(sketch, "E249.MirrorCS", {"start": v(1964.07, -1018.06) * mm, "end": v(1964.07, -1058.06) * mm});
            skLineSegment(sketch, "E250.MirrorCS", {"start": v(1732.07, -978.06) * mm, "end": v(1982.07, -978.06) * mm, "construction": true});
            skLineSegment(sketch, "E251.MirrorCS", {"start": v(1732.07, -838.06) * mm, "end": v(1750.07, -838.06) * mm});
            skLineSegment(sketch, "E252.MirrorCS", {"start": v(1624.3, -1067.82) * mm, "end": v(1624.3, -1085.82) * mm});
            skLineSegment(sketch, "E253.MirrorCS", {"start": v(1714.07, -1067.82) * mm, "end": v(1624.3, -1067.82) * mm});
            skLineSegment(sketch, "E254.MirrorCS", {"start": v(1714.07, -978.06) * mm, "end": v(1714.07, -1067.82) * mm});
            skLineSegment(sketch, "E255.MirrorCS", {"start": v(1732.07, -978.06) * mm, "end": v(1732.07, -878.06) * mm});
            skLineSegment(sketch, "E256.MirrorCS", {"start": v(2000.07, -458.06) * mm, "end": v(1982.07, -458.06) * mm});
            skLineSegment(sketch, "E257.MirrorCS", {"start": v(1664.3, -1085.82) * mm, "end": v(1664.3, -1099.08) * mm});
            skLineSegment(sketch, "E258.MirrorCS", {"start": v(1732.07, 61.94) * mm, "end": v(1750.07, 61.94) * mm});
            skLineSegment(sketch, "E259.MirrorCS", {"start": v(1664.3, -1085.82) * mm, "end": v(1704.3, -1085.82) * mm});
            skLineSegment(sketch, "E260.MirrorCS", {"start": v(1732.07, 101.94) * mm, "end": v(1750.07, 101.94) * mm});
            skLineSegment(sketch, "E261.MirrorCS", {"start": v(1982.07, 21.94) * mm, "end": v(2000.07, 21.94) * mm});
            skLineSegment(sketch, "E262.MirrorCS", {"start": v(1750.07, -1018.06) * mm, "end": v(1750.07, -1058.06) * mm});
            skLineSegment(sketch, "E263.MirrorCS", {"start": v(1982.07, -538.06) * mm, "end": v(1982.07, -498.06) * mm});
            skLineSegment(sketch, "E264.MirrorCS", {"start": v(1982.07, 61.94) * mm, "end": v(1982.07, 101.94) * mm});
            skLineSegment(sketch, "E265.MirrorCS", {"start": v(1732.07, -1018.06) * mm, "end": v(1732.07, -1058.06) * mm});
            skLineSegment(sketch, "E266.MirrorCS", {"start": v(2000.07, -978.06) * mm, "end": v(2000.07, -1103.83) * mm});
            skLineSegment(sketch, "E267.MirrorCS", {"start": v(1714.07, 21.94) * mm, "end": v(1714.07, 141.94) * mm});
            skLineSegment(sketch, "E268.MirrorCS", {"start": v(1982.07, -578.06) * mm, "end": v(2000.07, -578.06) * mm});
            skLineSegment(sketch, "E269.MirrorCS", {"start": v(1982.07, -458.06) * mm, "end": v(1982.07, -278.06) * mm});
            skLineSegment(sketch, "E270.MirrorCS", {"start": v(1962.07, -1317.82) * mm, "end": v(1982.07, -1317.82) * mm});
            skLineSegment(sketch, "E271.MirrorCS", {"start": v(1732.07, 21.94) * mm, "end": v(1714.07, 21.94) * mm});
            skLineSegment(sketch, "E272.MirrorCS", {"start": v(1624.3, -1085.82) * mm, "end": v(1524.3, -1085.82) * mm});
            skLineSegment(sketch, "E273.MirrorCS", {"start": v(1732.07, -158.06) * mm, "end": v(1732.07, 21.94) * mm});
            skLineSegment(sketch, "E274.MirrorCS", {"start": v(1750.07, 61.94) * mm, "end": v(1750.07, 101.94) * mm});
            skLineSegment(sketch, "E275.MirrorCS", {"start": v(1982.07, -758.06) * mm, "end": v(1982.07, -578.06) * mm});
            skLineSegment(sketch, "E276.MirrorCS", {"start": v(2000.07, 141.94) * mm, "end": v(1982.07, 141.94) * mm});
            skLineSegment(sketch, "E277.MirrorCS", {"start": v(1714.07, -458.06) * mm, "end": v(1732.07, -458.06) * mm});
            skLineSegment(sketch, "E278.MirrorCS", {"start": v(49.22, 2200.84) * mm, "end": v(40.22, 2185.25) * mm});
            skLineSegment(sketch, "E279.MirrorCS", {"start": v(1982.07, -158.06) * mm, "end": v(1982.07, 21.94) * mm});
            skLineSegment(sketch, "E280.MirrorCS", {"start": v(1732.07, 61.94) * mm, "end": v(1732.07, 101.94) * mm});
            skLineSegment(sketch, "E281.MirrorCS", {"start": v(2000.07, 21.94) * mm, "end": v(2000.07, 141.94) * mm});
            skLineSegment(sketch, "E282.MirrorCS", {"start": v(2000.07, -578.06) * mm, "end": v(2000.07, -458.06) * mm});
            skLineSegment(sketch, "E283.MirrorCS", {"start": v(1732.07, -538.06) * mm, "end": v(1750.07, -538.06) * mm});
            skLineSegment(sketch, "E284.MirrorCS", {"start": v(1937.07, -1285.82) * mm, "end": v(1937.07, -1335.82) * mm});
            skLineSegment(sketch, "E285.MirrorCS", {"start": v(1732.07, -498.06) * mm, "end": v(1750.07, -498.06) * mm});
            skLineSegment(sketch, "E286.MirrorCS", {"start": v(1732.07, -578.06) * mm, "end": v(1714.07, -578.06) * mm});
            skLineSegment(sketch, "E287.MirrorCS", {"start": v(1964.07, -538.06) * mm, "end": v(1964.07, -498.06) * mm});
            skLineSegment(sketch, "E288.MirrorCS", {"start": v(1962.74, 61.94) * mm, "end": v(1962.74, 101.94) * mm});
            skLineSegment(sketch, "E289.MirrorCS", {"start": v(1714.07, 141.94) * mm, "end": v(1732.07, 141.94) * mm});
            skLineSegment(sketch, "E290.MirrorCS", {"start": v(1744.3, -1335.82) * mm, "end": v(1777.07, -1335.82) * mm});
            skLineSegment(sketch, "E291.MirrorCS", {"start": v(144.14, 2125.25) * mm, "end": v(153.14, 2140.84) * mm});
            skLineSegment(sketch, "E292.MirrorCS", {"start": v(1744.3, -1353.82) * mm, "end": v(1744.3, -1335.82) * mm});
            skLineSegment(sketch, "E293.MirrorCS", {"start": v(1703, 1225.28) * mm, "end": v(1712, 1240.87) * mm});
            skLineSegment(sketch, "E294.MirrorCS", {"start": v(1624.3, -1353.82) * mm, "end": v(1744.3, -1353.82) * mm});
            skLineSegment(sketch, "E295.MirrorCS", {"start": v(1982.07, -1317.82) * mm, "end": v(1982.07, -1103.83) * mm});
            skLineSegment(sketch, "E296.MirrorCS", {"start": v(29.97, 2141.17) * mm, "end": v(20.97, 2141.17) * mm});
            skLineSegment(sketch, "E297.MirrorCS", {"start": v(29.97, 2191.16) * mm, "end": v(29.97, 2141.17) * mm});
            skLineSegment(sketch, "E298.MirrorCS", {"start": v(1732.07, -458.06) * mm, "end": v(1732.07, -278.06) * mm});
            skLineSegment(sketch, "E299.MirrorCS", {"start": v(1524.3, -1085.82) * mm, "end": v(1524.3, -1067.82) * mm});
            skLineSegment(sketch, "E300.MirrorCS", {"start": v(1962.07, -1335.82) * mm, "end": v(1962.07, -1317.82) * mm});
            skLineSegment(sketch, "E301.MirrorCS", {"start": v(40.22, 2185.25) * mm, "end": v(29.97, 2191.16) * mm});
            skLineSegment(sketch, "E302.MirrorCS", {"start": v(1750.07, -538.06) * mm, "end": v(1750.07, -498.06) * mm});
            skLineSegment(sketch, "E303.MirrorCS", {"start": v(1937.07, -1335.82) * mm, "end": v(1962.07, -1335.82) * mm});
            skLineSegment(sketch, "E304.MirrorCS", {"start": v(1058.39, 1308.76) * mm, "end": v(1049.39, 1293.17) * mm});
            skLineSegment(sketch, "E305.MirrorCS", {"start": v(1732.07, -538.06) * mm, "end": v(1732.07, -498.06) * mm});
            skLineSegment(sketch, "E306.MirrorCS", {"start": v(1714.07, -578.06) * mm, "end": v(1714.07, -458.06) * mm});
            skLineSegment(sketch, "E307.MirrorCS", {"start": v(1777.07, -1285.82) * mm, "end": v(1937.07, -1285.82) * mm});
            skLineSegment(sketch, "E308.MirrorCS", {"start": v(1578, 1008.77) * mm, "end": v(1569, 993.18) * mm});
            skLineSegment(sketch, "E309.MirrorCS", {"start": v(1777.07, -1335.82) * mm, "end": v(1777.07, -1285.82) * mm});
            skLineSegment(sketch, "E310.MirrorCS", {"start": v(153.14, 2140.84) * mm, "end": v(49.22, 2200.84) * mm});
            skLineSegment(sketch, "E311.MirrorCS", {"start": v(1732.07, -758.06) * mm, "end": v(1732.07, -578.06) * mm});
            skLineSegment(sketch, "E312.MirrorCS", {"start": v(663.76, 1825.26) * mm, "end": v(672.76, 1840.85) * mm});
            skLineSegment(sketch, "E313.MirrorCS", {"start": v(945.46, 1353.17) * mm, "end": v(954.46, 1368.76) * mm});
            skLineSegment(sketch, "E314.MirrorCS", {"start": v(1858.89, 1135.28) * mm, "end": v(1703, 1225.28) * mm});
            skLineSegment(sketch, "E315.MirrorCS", {"start": v(1624.3, -1335.82) * mm, "end": v(1624.3, -1353.82) * mm});
            skLineSegment(sketch, "E316.MirrorCS", {"start": v(1049.39, 1293.17) * mm, "end": v(945.46, 1353.17) * mm});
            skLineSegment(sketch, "E317.MirrorCS", {"start": v(1465.08, 1053.18) * mm, "end": v(1474.08, 1068.77) * mm});
            skLineSegment(sketch, "E318.MirrorCS", {"start": v(538.77, 1608.75) * mm, "end": v(529.77, 1593.16) * mm});
            skLineSegment(sketch, "E319.MirrorCS", {"start": v(1524.3, -1335.82) * mm, "end": v(1624.3, -1335.82) * mm});
            skLineSegment(sketch, "E320.MirrorCS", {"start": v(1569, 993.18) * mm, "end": v(1465.08, 1053.18) * mm});
            skLineSegment(sketch, "E321.MirrorCS", {"start": v(1524.3, -1353.82) * mm, "end": v(1524.3, -1335.82) * mm});
            skLineSegment(sketch, "E322.MirrorCS", {"start": v(1703, 1225.28) * mm, "end": v(1578, 1008.77) * mm, "construction": true});
            skLineSegment(sketch, "E323.MirrorCS", {"start": v(568.84, 1900.85) * mm, "end": v(559.84, 1885.26) * mm});
            skLineSegment(sketch, "E324.MirrorCS", {"start": v(924.3, -1353.82) * mm, "end": v(924.3, -1335.82) * mm});
            skLineSegment(sketch, "E325.MirrorCS", {"start": v(923.57, 1675.27) * mm, "end": v(932.57, 1690.85) * mm});
            skLineSegment(sketch, "E326.MirrorCS", {"start": v(685.65, 1503.17) * mm, "end": v(694.65, 1518.75) * mm});
            skLineSegment(sketch, "E327.MirrorCS", {"start": v(1443.2, 1375.28) * mm, "end": v(1452.2, 1390.86) * mm});
            skLineSegment(sketch, "E328.MirrorCS", {"start": v(804.3, -1335.82) * mm, "end": v(804.3, -1353.82) * mm});
            skLineSegment(sketch, "E329.MirrorCS", {"start": v(1608.08, 1300.87) * mm, "end": v(1599.08, 1285.28) * mm});
            skLineSegment(sketch, "E330.MirrorCS", {"start": v(672.76, 1840.85) * mm, "end": v(568.84, 1900.85) * mm});
            skLineSegment(sketch, "E331.MirrorCS", {"start": v(954.46, 1368.76) * mm, "end": v(798.58, 1458.76) * mm});
            skLineSegment(sketch, "E332.MirrorCS", {"start": v(204.3, -1335.82) * mm, "end": v(204.3, -1353.82) * mm});
            skLineSegment(sketch, "E333.MirrorCS", {"start": v(1712, 1240.87) * mm, "end": v(1608.08, 1300.87) * mm});
            skLineSegment(sketch, "E334.MirrorCS", {"start": v(278.95, 1758.75) * mm, "end": v(269.96, 1743.16) * mm});
            skLineSegment(sketch, "E335.MirrorCS", {"start": v(624.3, -1353.82) * mm, "end": v(624.3, -1335.82) * mm});
            skLineSegment(sketch, "E336.MirrorCS", {"start": v(819.65, 1735.26) * mm, "end": v(663.76, 1825.26) * mm});
            skLineSegment(sketch, "E337.MirrorCS", {"start": v(434.84, 1668.75) * mm, "end": v(278.95, 1758.75) * mm});
            skLineSegment(sketch, "E338.MirrorCS", {"start": v(1205.27, 1203.18) * mm, "end": v(1214.27, 1218.77) * mm});
            skLineSegment(sketch, "E339.MirrorCS", {"start": v(1079.46, 1585.27) * mm, "end": v(923.57, 1675.27) * mm});
            skLineSegment(sketch, "E340.MirrorCS", {"start": v(425.84, 1653.16) * mm, "end": v(434.84, 1668.75) * mm});
            skLineSegment(sketch, "E341.MirrorCS", {"start": v(828.65, 1750.85) * mm, "end": v(819.65, 1735.26) * mm});
            skLineSegment(sketch, "E342.MirrorCS", {"start": v(504.3, -1335.82) * mm, "end": v(504.3, -1353.82) * mm});
            skLineSegment(sketch, "E343.MirrorCS", {"start": v(1309.2, 1143.18) * mm, "end": v(1205.27, 1203.18) * mm});
            skLineSegment(sketch, "E344.MirrorCS", {"start": v(789.58, 1443.17) * mm, "end": v(685.65, 1503.17) * mm});
            skLineSegment(sketch, "E345.MirrorCS", {"start": v(529.77, 1593.16) * mm, "end": v(425.84, 1653.16) * mm});
            skLineSegment(sketch, "E346.MirrorCS", {"start": v(1088.46, 1600.86) * mm, "end": v(1079.46, 1585.27) * mm});
            skLineSegment(sketch, "E347.MirrorCS", {"start": v(924.3, -1085.82) * mm, "end": v(924.3, -1067.82) * mm});
            skLineSegment(sketch, "E348.MirrorCS", {"start": v(1524.3, -1067.82) * mm, "end": v(1404.3, -1067.82) * mm});
            skLineSegment(sketch, "E349.MirrorCS", {"start": v(804.3, -1067.82) * mm, "end": v(804.3, -1085.82) * mm});
            skLineSegment(sketch, "E350.MirrorCS", {"start": v(924.3, -1067.82) * mm, "end": v(804.3, -1067.82) * mm});
            skLineSegment(sketch, "E351.MirrorCS", {"start": v(798.58, 1458.76) * mm, "end": v(789.58, 1443.17) * mm});
            skLineSegment(sketch, "E352.MirrorCS", {"start": v(1318.2, 1158.77) * mm, "end": v(1309.2, 1143.18) * mm});
            skLineSegment(sketch, "E353.MirrorCS", {"start": v(204.3, -1067.82) * mm, "end": v(204.3, -1085.82) * mm});
            skLineSegment(sketch, "E354.MirrorCS", {"start": v(100.98, -1335.82) * mm, "end": v(100.98, -1285.82) * mm});
            skLineSegment(sketch, "E355.MirrorCS", {"start": v(932.57, 1690.85) * mm, "end": v(828.65, 1750.85) * mm});
            skLineSegment(sketch, "E356.MirrorCS", {"start": v(694.65, 1518.75) * mm, "end": v(538.77, 1608.75) * mm});
            skLineSegment(sketch, "E357.MirrorCS", {"start": v(1452.2, 1390.86) * mm, "end": v(1348.27, 1450.86) * mm});
            skLineSegment(sketch, "E358.MirrorCS", {"start": v(804.3, -1353.82) * mm, "end": v(924.3, -1353.82) * mm});
            skLineSegment(sketch, "E359.MirrorCS", {"start": v(1183.38, 1525.27) * mm, "end": v(1192.38, 1540.86) * mm});
            skLineSegment(sketch, "E360.MirrorCS", {"start": v(166.03, 1803.16) * mm, "end": v(175.03, 1818.74) * mm});
            skLineSegment(sketch, "E361.MirrorCS", {"start": v(324.3, -1067.82) * mm, "end": v(204.3, -1067.82) * mm});
            skLineSegment(sketch, "E362.MirrorCS", {"start": v(1192.38, 1540.86) * mm, "end": v(1088.46, 1600.86) * mm});
            skLineSegment(sketch, "E363.MirrorCS", {"start": v(204.3, -1335.82) * mm, "end": v(100.98, -1335.82) * mm});
            skLineSegment(sketch, "E364.MirrorCS", {"start": v(204.3, -1353.82) * mm, "end": v(324.3, -1353.82) * mm});
            skLineSegment(sketch, "E365.MirrorCS", {"start": v(1339.27, 1435.27) * mm, "end": v(1183.38, 1525.27) * mm});
            skLineSegment(sketch, "E366.MirrorCS", {"start": v(324.3, -1085.82) * mm, "end": v(324.3, -1067.82) * mm});
            skLineSegment(sketch, "E367.MirrorCS", {"start": v(269.96, 1743.16) * mm, "end": v(166.03, 1803.16) * mm});
            skLineSegment(sketch, "E368.MirrorCS", {"start": v(1404.3, -1335.82) * mm, "end": v(1404.3, -1353.82) * mm});
            skLineSegment(sketch, "E369.MirrorCS", {"start": v(1474.08, 1068.77) * mm, "end": v(1318.2, 1158.77) * mm});
            skLineSegment(sketch, "E370.MirrorCS", {"start": v(1348.27, 1450.86) * mm, "end": v(1339.27, 1435.27) * mm});
            skLineSegment(sketch, "E371.MirrorCS", {"start": v(663.76, 1825.26) * mm, "end": v(538.77, 1608.75) * mm, "construction": true});
            skLineSegment(sketch, "E372.MirrorCS", {"start": v(1214.27, 1218.77) * mm, "end": v(1058.39, 1308.76) * mm});
            skLineSegment(sketch, "E373.MirrorCS", {"start": v(1224.3, -1335.82) * mm, "end": v(1404.3, -1335.82) * mm});
            skLineSegment(sketch, "E374.MirrorCS", {"start": v(504.3, -1353.82) * mm, "end": v(624.3, -1353.82) * mm});
            skLineSegment(sketch, "E375.MirrorCS", {"start": v(624.3, -1067.82) * mm, "end": v(504.3, -1067.82) * mm});
            skLineSegment(sketch, "E376.MirrorCS", {"start": v(504.3, -1067.82) * mm, "end": v(504.3, -1085.82) * mm});
            skLineSegment(sketch, "E377.MirrorCS", {"start": v(1224.3, -1353.82) * mm, "end": v(1224.3, -1335.82) * mm});
            skLineSegment(sketch, "E378.MirrorCS", {"start": v(309.03, 2050.84) * mm, "end": v(300.03, 2035.25) * mm});
            skLineSegment(sketch, "E379.MirrorCS", {"start": v(1104.3, -1353.82) * mm, "end": v(1224.3, -1353.82) * mm});
            skLineSegment(sketch, "E380.MirrorCS", {"start": v(204.3, -1085.82) * mm, "end": v(80.98, -1085.82) * mm});
            skLineSegment(sketch, "E381.MirrorCS", {"start": v(1732.07, 321.94) * mm, "end": v(1714.07, 321.94) * mm});
            skLineSegment(sketch, "E382.MirrorCS", {"start": v(1104.3, -1067.82) * mm, "end": v(1104.3, -1085.82) * mm});
            skLineSegment(sketch, "E383.MirrorCS", {"start": v(1224.3, -1085.82) * mm, "end": v(1224.3, -1067.82) * mm});
            skLineSegment(sketch, "E384.MirrorCS", {"start": v(1404.3, -1067.82) * mm, "end": v(1404.3, -1085.82) * mm});
            skLineSegment(sketch, "E385.MirrorCS", {"start": v(1982.07, 921.94) * mm, "end": v(2000.07, 921.94) * mm});
            skLineSegment(sketch, "E386.MirrorCS", {"start": v(1714.07, 441.94) * mm, "end": v(1732.07, 441.94) * mm});
            skLineSegment(sketch, "E387.MirrorCS", {"start": v(324.3, -1353.82) * mm, "end": v(324.3, -1335.82) * mm});
            skLineSegment(sketch, "E388.MirrorCS", {"start": v(559.84, 1885.26) * mm, "end": v(403.95, 1975.26) * mm});
            skLineSegment(sketch, "E389.MirrorCS", {"start": v(1404.3, -1353.82) * mm, "end": v(1524.3, -1353.82) * mm});
            skLineSegment(sketch, "E390.MirrorCS", {"start": v(2000.07, 441.94) * mm, "end": v(1982.07, 441.94) * mm});
            skLineSegment(sketch, "E391.MirrorCS", {"start": v(1732.07, 141.94) * mm, "end": v(1732.07, 321.94) * mm});
            skLineSegment(sketch, "E392.MirrorCS", {"start": v(1714.07, 321.94) * mm, "end": v(1714.07, 441.94) * mm});
            skLineSegment(sketch, "E393.MirrorCS", {"start": v(624.3, -1335.82) * mm, "end": v(804.3, -1335.82) * mm});
            skLineSegment(sketch, "E394.MirrorCS", {"start": v(504.3, -1085.82) * mm, "end": v(324.3, -1085.82) * mm});
            skLineSegment(sketch, "E395.MirrorCS", {"start": v(2000.07, 741.94) * mm, "end": v(1982.07, 741.94) * mm});
            skLineSegment(sketch, "E396.MirrorCS", {"start": v(1599.08, 1285.28) * mm, "end": v(1443.2, 1375.28) * mm});
            skLineSegment(sketch, "E397.MirrorCS", {"start": v(2000.07, 321.94) * mm, "end": v(2000.07, 441.94) * mm});
            skLineSegment(sketch, "E398.MirrorCS", {"start": v(2000.07, 621.94) * mm, "end": v(2000.07, 741.94) * mm});
            skLineSegment(sketch, "E399.MirrorCS", {"start": v(300.03, 2035.25) * mm, "end": v(144.14, 2125.25) * mm});
            skLineSegment(sketch, "E400.MirrorCS", {"start": v(1982.07, 621.94) * mm, "end": v(2000.07, 621.94) * mm});
            skLineSegment(sketch, "E401.MirrorCS", {"start": v(624.3, -1085.82) * mm, "end": v(624.3, -1067.82) * mm});
            skLineSegment(sketch, "E402.MirrorCS", {"start": v(2000.07, 921.94) * mm, "end": v(2000.07, 1041.94) * mm});
            skLineSegment(sketch, "E403.MirrorCS", {"start": v(1982.07, 321.94) * mm, "end": v(2000.07, 321.94) * mm});
            skLineSegment(sketch, "E404.MirrorCS", {"start": v(1982.07, 141.94) * mm, "end": v(1982.07, 321.94) * mm});
            skLineSegment(sketch, "E405.MirrorCS", {"start": v(1732.07, 441.94) * mm, "end": v(1732.07, 621.94) * mm});
            skLineSegment(sketch, "E406.MirrorCS", {"start": v(1104.3, -1085.82) * mm, "end": v(924.3, -1085.82) * mm});
            skLineSegment(sketch, "E407.MirrorCS", {"start": v(1224.3, -1067.82) * mm, "end": v(1104.3, -1067.82) * mm});
            skLineSegment(sketch, "E408.MirrorCS", {"start": v(100.98, -1285.82) * mm, "end": v(20.98, -1285.82) * mm});
            skLineSegment(sketch, "E409.MirrorCS", {"start": v(1404.3, -1085.82) * mm, "end": v(1224.3, -1085.82) * mm});
            skLineSegment(sketch, "E410.MirrorCS", {"start": v(804.3, -1085.82) * mm, "end": v(624.3, -1085.82) * mm});
            skLineSegment(sketch, "E411.MirrorCS", {"start": v(412.95, 1990.84) * mm, "end": v(309.03, 2050.84) * mm});
            skLineSegment(sketch, "E412.MirrorCS", {"start": v(1104.3, -1335.82) * mm, "end": v(1104.3, -1353.82) * mm});
            skLineSegment(sketch, "E413.MirrorCS", {"start": v(324.3, -1335.82) * mm, "end": v(504.3, -1335.82) * mm});
            skLineSegment(sketch, "E414.MirrorCS", {"start": v(403.95, 1975.26) * mm, "end": v(412.95, 1990.84) * mm});
            skLineSegment(sketch, "E415.MirrorCS", {"start": v(924.3, -1335.82) * mm, "end": v(1104.3, -1335.82) * mm});
            skLineSegment(sketch, "E416.MirrorCS", {"start": v(1982.07, 741.94) * mm, "end": v(1982.07, 921.94) * mm});
            skLineSegment(sketch, "E417.MirrorCS", {"start": v(1982.07, 441.94) * mm, "end": v(1982.07, 621.94) * mm});
            skLineSegment(sketch, "E418.MirrorCS", {"start": v(1714.07, 621.94) * mm, "end": v(1714.07, 741.94) * mm});
            skLineSegment(sketch, "E419.MirrorCS", {"start": v(1714.07, 741.94) * mm, "end": v(1732.07, 741.94) * mm});
            skLineSegment(sketch, "E420.MirrorCS", {"start": v(1732.07, 621.94) * mm, "end": v(1714.07, 621.94) * mm});
            skLineSegment(sketch, "E421.MirrorCS", {"start": v(1578, 1008.77) * mm, "end": v(1732.07, 919.83) * mm});
            skLineSegment(sketch, "E422.MirrorCS", {"start": v(1732.07, 741.94) * mm, "end": v(1732.07, 919.83) * mm});
            skLineSegment(sketch, "E423.MirrorCS", {"start": v(175.03, 1818.74) * mm, "end": v(20.97, 1907.69) * mm});
            skPoint(sketch, "E424.MirrorP", {"position": v(1982.07, -218.06) * mm});
            skPoint(sketch, "E425.MirrorP", {"position": v(1732.07, -218.06) * mm});
            skLineSegment(sketch, "E426", {"start": v(-1527.04, 993.18) * mm, "end": v(-1690.1, 899.05) * mm, "construction": true});
            skLineSegment(sketch, "E427", {"start": v(-1672.1, 741.94) * mm, "end": v(-1672.1, 930.22) * mm, "construction": true});
            skPoint(sketch, "E428", {"position": v(-1672.1, 909.44) * mm});
            skPoint(sketch, "E429", {"position": v(-1672.1, 864.44) * mm});
            skLineSegment(sketch, "E430", {"start": v(-124.06, 1803.16) * mm, "end": v(38.99, 1897.29) * mm, "construction": true});
            skLineSegment(sketch, "E431", {"start": v(166.03, 1803.16) * mm, "end": v(2.98, 1897.29) * mm, "construction": true});
            skPoint(sketch, "E432", {"position": v(20.98, 1886.9) * mm});
            skLineSegment(sketch, "E433", {"start": v(-7.25, 2200.84) * mm, "end": v(20.98, 2217.14) * mm, "construction": true});
            skLineSegment(sketch, "E434", {"start": v(49.22, 2200.84) * mm, "end": v(20.98, 2217.14) * mm, "construction": true});
            skLineSegment(sketch, "E435", {"start": v(-1929.84, 1090.88) * mm, "end": v(-1958.1, 1074.56) * mm, "construction": true});
            skLineSegment(sketch, "E436", {"start": v(-1958.1, 1074.56) * mm, "end": v(-1958.1, 1041.94) * mm, "construction": true});
            skLineSegment(sketch, "E437", {"start": v(-1702.33, -1353.82) * mm, "end": v(-1958.1, -1353.82) * mm, "construction": true});
            skLineSegment(sketch, "E438", {"start": v(-452.1, -1067.82) * mm, "end": v(-452.1, -383.6) * mm, "construction": true});
            skLineSegment(sketch, "E439", {"start": v(494.07, -1067.82) * mm, "end": v(494.07, 1372.18) * mm, "construction": true});
            skLineSegment(sketch, "E440", {"start": v(1465.08, 1053.18) * mm, "end": v(166.03, 1803.16) * mm, "construction": true});
            skLineSegment(sketch, "E441", {"start": v(494.07, 1372.18) * mm, "end": v(912.55, 1372.18) * mm, "construction": true});
            skLineSegment(sketch, "E442", {"start": v(912.55, 1372.18) * mm, "end": v(912.55, -1067.82) * mm, "construction": true});
            skLineSegment(sketch, "E443", {"start": v(-1672.1, 909.44) * mm, "end": v(-1672.1, -978.06) * mm});
            skLineSegment(sketch, "E444", {"start": v(-1582.33, -1067.82) * mm, "end": v(1624.3, -1067.82) * mm});
            skLineSegment(sketch, "E445", {"start": v(1714.07, -978.06) * mm, "end": v(1714.07, 909.44) * mm});
            skLineSegment(sketch, "E446", {"start": v(20.98, 1886.9) * mm, "end": v(1714.07, 909.44) * mm});
            skLineSegment(sketch, "E447", {"start": v(20.98, 1886.9) * mm, "end": v(-1672.1, 909.44) * mm});
            skSolve(sketch);
        }
        {
            var Q0;
            Q0=makeQuery(id+"F0.imprint","IMPRINT",FACE,{"disambiguationData":[TD([[makeQuery(id+"F0.imprint","IMPRINT",EDGE,{"derivedFrom":sQuery(id+"F0.wireOp",EDGE,"E0")}),-1.0]])]});
            var Q1;
            {var subQ0=sQuery(id+"F0.wireOp",EDGE,"E6");Q1=makeQuery(id+"F0.imprint","IMPRINT",FACE,{"disambiguationData":[TD([[makeQuery(id+"F0.imprint","IMPRINT",EDGE,{"derivedFrom":subQ0}),1.0]])]});}
            var Q2;
            {var subQ0=sQuery(id+"F0.wireOp",EDGE,"E2");Q2=makeQuery(id+"F0.imprint","IMPRINT",FACE,{"disambiguationData":[TD([[makeQuery(id+"F0.imprint","IMPRINT",EDGE,{"derivedFrom":subQ0}),1.0]])]});}
            var Q3;
            {var subQ0=sQuery(id+"F0.wireOp",EDGE,"E10");Q3=makeQuery(id+"F0.imprint","IMPRINT",FACE,{"disambiguationData":[TD([[makeQuery(id+"F0.imprint","IMPRINT",EDGE,{"derivedFrom":subQ0}),1.0]])]});}
            var Q4;
            {var subQ0=sQuery(id+"F0.wireOp",EDGE,"E14");Q4=makeQuery(id+"F0.imprint","IMPRINT",FACE,{"disambiguationData":[TD([[makeQuery(id+"F0.imprint","IMPRINT",EDGE,{"derivedFrom":subQ0}),1.0]])]});}
            var Q5;
            {var subQ0=sQuery(id+"F0.wireOp",EDGE,"E18");Q5=makeQuery(id+"F0.imprint","IMPRINT",FACE,{"disambiguationData":[TD([[makeQuery(id+"F0.imprint","IMPRINT",EDGE,{"derivedFrom":subQ0}),1.0]])]});}
            var Q6;
            {var subQ0=sQuery(id+"F0.wireOp",EDGE,"E22");Q6=makeQuery(id+"F0.imprint","IMPRINT",FACE,{"disambiguationData":[TD([[makeQuery(id+"F0.imprint","IMPRINT",EDGE,{"derivedFrom":subQ0}),1.0]])]});}
            var Q7;
            {var subQ0=sQuery(id+"F0.wireOp",EDGE,"E207.MirrorCS");Q7=makeQuery(id+"F0.imprint","IMPRINT",FACE,{"disambiguationData":[TD([[makeQuery(id+"F0.imprint","IMPRINT",EDGE,{"derivedFrom":subQ0}),-1.0]])]});}
            var Q8;
            {var subQ0=sQuery(id+"F0.wireOp",EDGE,"E366.MirrorCS");Q8=makeQuery(id+"F0.imprint","IMPRINT",FACE,{"disambiguationData":[TD([[makeQuery(id+"F0.imprint","IMPRINT",EDGE,{"derivedFrom":subQ0}),-1.0]])]});}
            var Q9;
            {var subQ0=sQuery(id+"F0.wireOp",EDGE,"E349.MirrorCS");Q9=makeQuery(id+"F0.imprint","IMPRINT",FACE,{"disambiguationData":[TD([[makeQuery(id+"F0.imprint","IMPRINT",EDGE,{"derivedFrom":subQ0}),-1.0]])]});}
            var Q10;
            {var subQ0=sQuery(id+"F0.wireOp",EDGE,"E347.MirrorCS");Q10=makeQuery(id+"F0.imprint","IMPRINT",FACE,{"disambiguationData":[TD([[makeQuery(id+"F0.imprint","IMPRINT",EDGE,{"derivedFrom":subQ0}),-1.0]])]});}
            var Q11;
            {var subQ0=sQuery(id+"F0.wireOp",EDGE,"E383.MirrorCS");Q11=makeQuery(id+"F0.imprint","IMPRINT",FACE,{"disambiguationData":[TD([[makeQuery(id+"F0.imprint","IMPRINT",EDGE,{"derivedFrom":subQ0}),-1.0]])]});}
            var Q12;
            {var subQ0=sQuery(id+"F0.wireOp",EDGE,"E252.MirrorCS");Q12=makeQuery(id+"F0.imprint","IMPRINT",FACE,{"disambiguationData":[TD([[makeQuery(id+"F0.imprint","IMPRINT",EDGE,{"derivedFrom":subQ0}),-1.0]])]});}
            var Q13;
            {var subQ0=sQuery(id+"F0.wireOp",EDGE,"E235.MirrorCS");Q13=makeQuery(id+"F0.imprint","IMPRINT",FACE,{"disambiguationData":[TD([[makeQuery(id+"F0.imprint","IMPRINT",EDGE,{"derivedFrom":subQ0}),1.0]])]});}
            var Q14;
            {var subQ0=sQuery(id+"F0.wireOp",EDGE,"E244.MirrorCS");Q14=makeQuery(id+"F0.imprint","IMPRINT",FACE,{"disambiguationData":[TD([[makeQuery(id+"F0.imprint","IMPRINT",EDGE,{"derivedFrom":subQ0}),1.0]])]});}
            var Q15;
            {var subQ0=sQuery(id+"F0.wireOp",EDGE,"E210.MirrorCS");Q15=makeQuery(id+"F0.imprint","IMPRINT",FACE,{"disambiguationData":[TD([[makeQuery(id+"F0.imprint","IMPRINT",EDGE,{"derivedFrom":subQ0}),1.0]])]});}
            var Q16;
            {var subQ0=sQuery(id+"F0.wireOp",EDGE,"E215.MirrorCS");Q16=makeQuery(id+"F0.imprint","IMPRINT",FACE,{"disambiguationData":[TD([[makeQuery(id+"F0.imprint","IMPRINT",EDGE,{"derivedFrom":subQ0}),1.0]])]});}
            var Q17;
            {var subQ0=sQuery(id+"F0.wireOp",EDGE,"E289.MirrorCS");Q17=makeQuery(id+"F0.imprint","IMPRINT",FACE,{"disambiguationData":[TD([[makeQuery(id+"F0.imprint","IMPRINT",EDGE,{"derivedFrom":subQ0}),1.0]])]});}
            var Q18;
            {var subQ0=sQuery(id+"F0.wireOp",EDGE,"E386.MirrorCS");Q18=makeQuery(id+"F0.imprint","IMPRINT",FACE,{"disambiguationData":[TD([[makeQuery(id+"F0.imprint","IMPRINT",EDGE,{"derivedFrom":subQ0}),1.0]])]});}
            var Q19;
            {var subQ0=sQuery(id+"F0.wireOp",EDGE,"E308.MirrorCS");Q19=makeQuery(id+"F0.imprint","IMPRINT",FACE,{"disambiguationData":[TD([[makeQuery(id+"F0.imprint","IMPRINT",EDGE,{"derivedFrom":subQ0}),1.0]])]});}
            var Q20;
            {var subQ0=sQuery(id+"F0.wireOp",EDGE,"E317.MirrorCS");Q20=makeQuery(id+"F0.imprint","IMPRINT",FACE,{"disambiguationData":[TD([[makeQuery(id+"F0.imprint","IMPRINT",EDGE,{"derivedFrom":subQ0}),1.0]])]});}
            var Q21;
            {var subQ0=sQuery(id+"F0.wireOp",EDGE,"E304.MirrorCS");Q21=makeQuery(id+"F0.imprint","IMPRINT",FACE,{"disambiguationData":[TD([[makeQuery(id+"F0.imprint","IMPRINT",EDGE,{"derivedFrom":subQ0}),1.0]])]});}
            var Q22;
            {var subQ0=sQuery(id+"F0.wireOp",EDGE,"E313.MirrorCS");Q22=makeQuery(id+"F0.imprint","IMPRINT",FACE,{"disambiguationData":[TD([[makeQuery(id+"F0.imprint","IMPRINT",EDGE,{"derivedFrom":subQ0}),1.0]])]});}
            var Q23;
            {var subQ0=sQuery(id+"F0.wireOp",EDGE,"E318.MirrorCS");Q23=makeQuery(id+"F0.imprint","IMPRINT",FACE,{"disambiguationData":[TD([[makeQuery(id+"F0.imprint","IMPRINT",EDGE,{"derivedFrom":subQ0}),1.0]])]});}
            var Q24;
            {var subQ0=sQuery(id+"F0.wireOp",EDGE,"E334.MirrorCS");Q24=makeQuery(id+"F0.imprint","IMPRINT",FACE,{"disambiguationData":[TD([[makeQuery(id+"F0.imprint","IMPRINT",EDGE,{"derivedFrom":subQ0}),1.0]])]});}
            var Q25;
            {var subQ4=sQuery(id+"F0.wireOp",EDGE,"E152");Q25=makeQuery(id+"F0.imprint","IMPRINT",FACE,{"disambiguationData":[TD([[makeQuery(id+"F0.imprint","IMPRINT",EDGE,{"derivedFrom":subQ4}),-1.0]])]});}
            var Q26;
            {var subQ0=sQuery(id+"F0.wireOp",EDGE,"E148");Q26=makeQuery(id+"F0.imprint","IMPRINT",FACE,{"disambiguationData":[TD([[makeQuery(id+"F0.imprint","IMPRINT",EDGE,{"derivedFrom":subQ0}),-1.0]])]});}
            var Q27;
            {var subQ0=sQuery(id+"F0.wireOp",EDGE,"E144");Q27=makeQuery(id+"F0.imprint","IMPRINT",FACE,{"disambiguationData":[TD([[makeQuery(id+"F0.imprint","IMPRINT",EDGE,{"derivedFrom":subQ0}),-1.0]])]});}
            var Q28;
            {var subQ0=sQuery(id+"F0.wireOp",EDGE,"E126");Q28=makeQuery(id+"F0.imprint","IMPRINT",FACE,{"disambiguationData":[TD([[makeQuery(id+"F0.imprint","IMPRINT",EDGE,{"derivedFrom":subQ0}),-1.0]])]});}
            var Q29;
            {var subQ0=sQuery(id+"F0.wireOp",EDGE,"E116");Q29=makeQuery(id+"F0.imprint","IMPRINT",FACE,{"disambiguationData":[TD([[makeQuery(id+"F0.imprint","IMPRINT",EDGE,{"derivedFrom":subQ0}),-1.0]])]});}
            var Q30;
            {var subQ0=sQuery(id+"F0.wireOp",EDGE,"E107");Q30=makeQuery(id+"F0.imprint","IMPRINT",FACE,{"disambiguationData":[TD([[makeQuery(id+"F0.imprint","IMPRINT",EDGE,{"derivedFrom":subQ0}),-1.0]])]});}
            var Q31;
            {var subQ4=sQuery(id+"F0.wireOp",EDGE,"E89");Q31=makeQuery(id+"F0.imprint","IMPRINT",FACE,{"disambiguationData":[TD([[makeQuery(id+"F0.imprint","IMPRINT",EDGE,{"derivedFrom":subQ4}),-1.0]])]});}
            var Q32;
            {var subQ0=sQuery(id+"F0.wireOp",EDGE,"E82");Q32=makeQuery(id+"F0.imprint","IMPRINT",FACE,{"disambiguationData":[TD([[makeQuery(id+"F0.imprint","IMPRINT",EDGE,{"derivedFrom":subQ0}),-1.0]])]});}
            var Q33;
            {var subQ0=sQuery(id+"F0.wireOp",EDGE,"E63");Q33=makeQuery(id+"F0.imprint","IMPRINT",FACE,{"disambiguationData":[TD([[makeQuery(id+"F0.imprint","IMPRINT",EDGE,{"derivedFrom":subQ0}),-1.0]])]});}
            var Q34;
            {var subQ0=sQuery(id+"F0.wireOp",EDGE,"E68");Q34=makeQuery(id+"F0.imprint","IMPRINT",FACE,{"disambiguationData":[TD([[makeQuery(id+"F0.imprint","IMPRINT",EDGE,{"derivedFrom":subQ0}),-1.0]])]});}
            var Q35;
            {var subQ0=sQuery(id+"F0.wireOp",EDGE,"E35");Q35=makeQuery(id+"F0.imprint","IMPRINT",FACE,{"disambiguationData":[TD([[makeQuery(id+"F0.imprint","IMPRINT",EDGE,{"derivedFrom":subQ0}),-1.0]])]});}
            var Q36;
            {var subQ0=sQuery(id+"F0.wireOp",EDGE,"E31");Q36=makeQuery(id+"F0.imprint","IMPRINT",FACE,{"disambiguationData":[TD([[makeQuery(id+"F0.imprint","IMPRINT",EDGE,{"derivedFrom":subQ0}),-1.0]])]});}
            var Q37;
            {var subQ0=sQuery(id+"F0.wireOp",EDGE,"E27");Q37=makeQuery(id+"F0.imprint","IMPRINT",FACE,{"disambiguationData":[TD([[makeQuery(id+"F0.imprint","IMPRINT",EDGE,{"derivedFrom":subQ0}),-1.0]])]});}
            extrude(context, id + "F1", {"entities" : qUnion([Q0, Q1, Q2, Q3, Q4, Q5, Q6, Q7, Q8, Q9, Q10, Q11, Q12, Q13, Q14, Q15, Q16, Q17, Q18, Q19, Q20, Q21, Q22, Q23, Q24, Q25, Q26, Q27, Q28, Q29, Q30, Q31, Q32, Q33, Q34, Q35, Q36, Q37]), "depth" : 4800 * mm});
        }
    });
